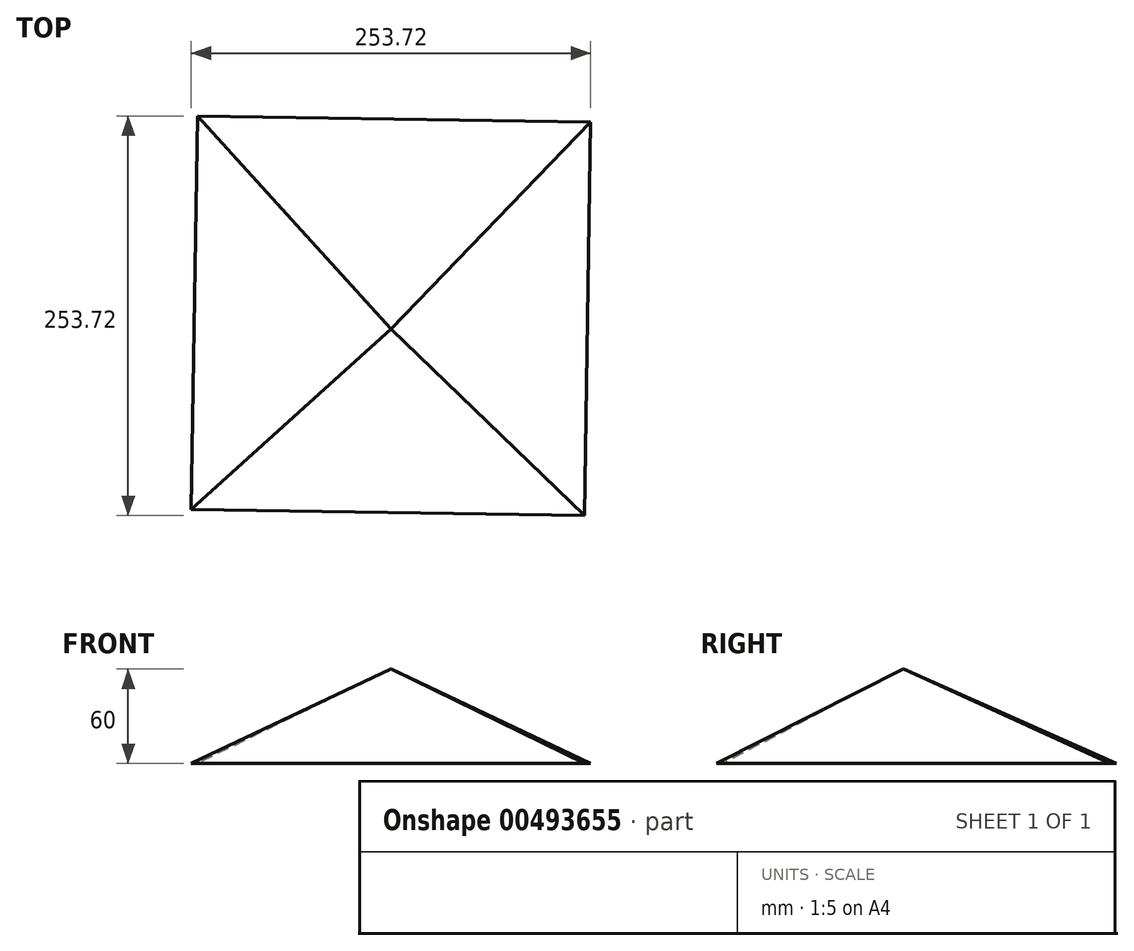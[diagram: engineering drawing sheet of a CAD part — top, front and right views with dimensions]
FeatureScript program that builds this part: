
annotation { "Feature Type Name" : "Feature", "Feature Type Description" : "" }
export const myFeature = defineFeature(function(context is Context, id is Id, definition is map)
    precondition{}
    {
        {
            var Q0;
            Q0=qCreatedBy(makeId("Top.planeOp"),FACE);
            var sketch = newSketch(context, id + "F0", { "sketchPlane" : qUnion([Q0])});
            skCircle(sketch, "E0.cCircle", {"center": v(0, 0) * mm, "radius": 124.9 * mm, "construction": true});
            skLineSegment(sketch, "E0.0", {"start": v(-122.9, 126.86) * mm, "end": v(126.86, 122.9) * mm});
            skLineSegment(sketch, "E0.1", {"start": v(126.86, 122.9) * mm, "end": v(122.9, -126.86) * mm});
            skLineSegment(sketch, "E0.2", {"start": v(122.9, -126.86) * mm, "end": v(-126.86, -122.9) * mm});
            skLineSegment(sketch, "E0.3", {"start": v(-126.86, -122.9) * mm, "end": v(-122.9, 126.86) * mm});
            skPoint(sketch, "E0.0.midPoint", {"position": v(1.98, 124.88) * mm});
            skSolve(sketch);
        }
        {
            var Q0;
            Q0=qCreatedBy(makeId("Top.planeOp"),FACE);
            cPlane(context, id + "F1", {"entities" : qUnion([Q0]), "cplaneType" : CPlaneType.OFFSET, "offset" : 60 * mm, "width" : 150 * mm, "height" : 150 * mm});
        }
        {
            var Q0;
            Q0=qCreatedBy(id+"F1.planeOp",FACE);
            var sketch = newSketch(context, id + "F2", { "sketchPlane" : qUnion([Q0])});
            skPoint(sketch, "E1", {"position": v(0, -8.4) * mm});
            skSolve(sketch);
        }
        {
            var Q0;
            Q0=sQuery(id+"F2.wireOp",VERTEX,"E1");
            var Q1;
            Q1=makeQuery(id+"F0.imprint","IMPRINT",FACE,{"disambiguationData":[TD([[makeQuery(id+"F0.imprint","IMPRINT",EDGE,{"derivedFrom":sQuery(id+"F0.wireOp",EDGE,"E0.0")}),-1.0]])]});
            loft(context, id + "F3", {"sheetProfilesArray" : [{ "sheetProfileEntities" : qUnion([Q0]) }, { "sheetProfileEntities" : qUnion([Q1]) }]});
        }
    });
